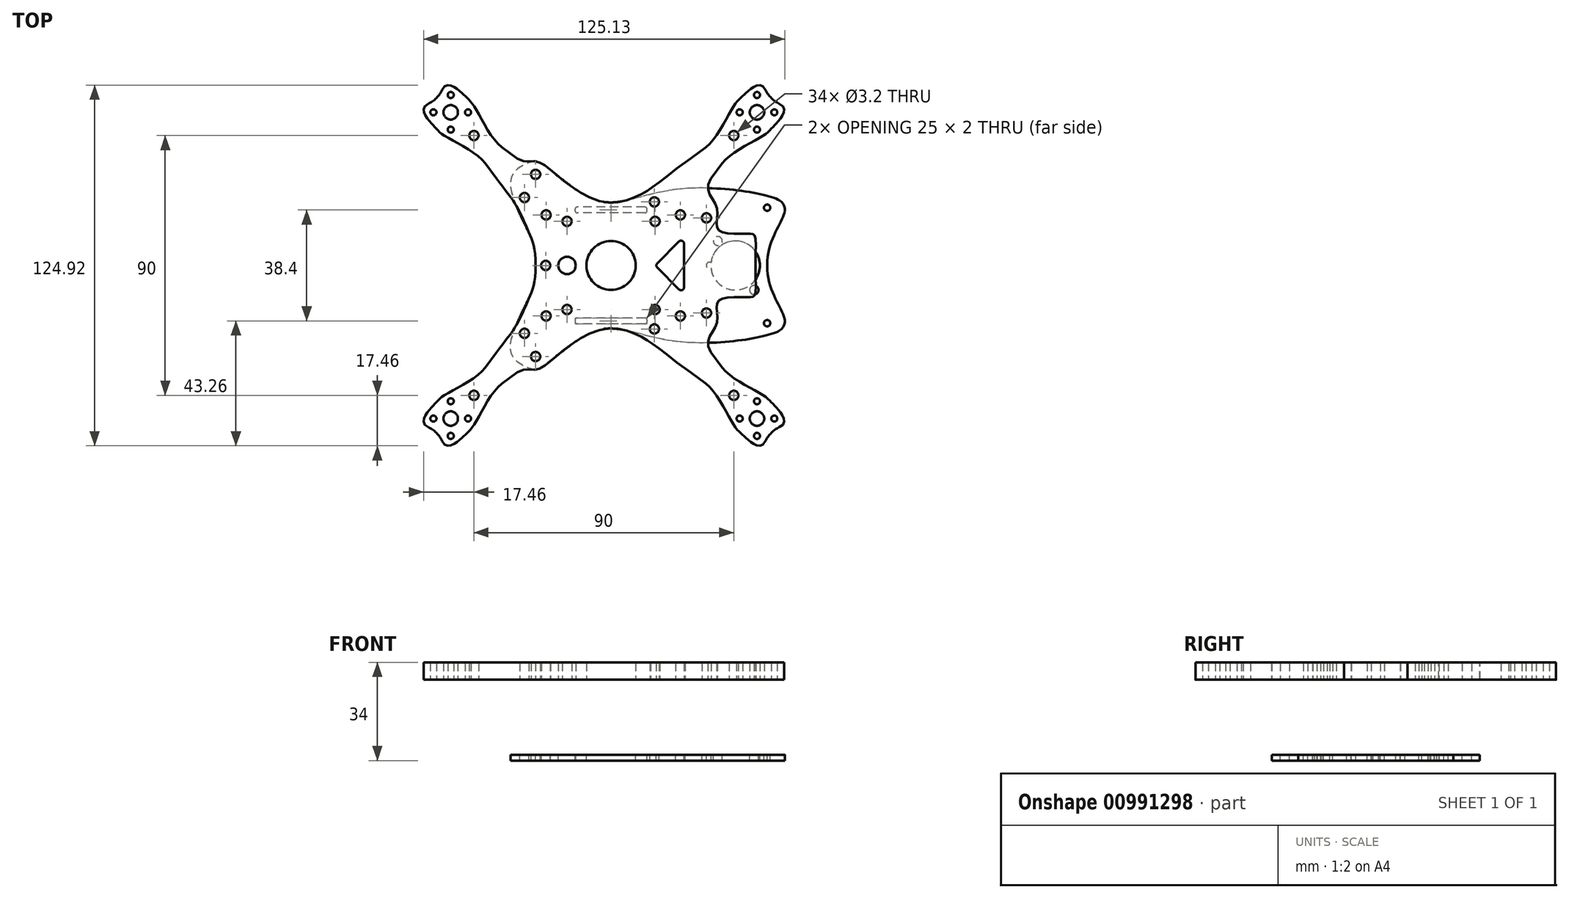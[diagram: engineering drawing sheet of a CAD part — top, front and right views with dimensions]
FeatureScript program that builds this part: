
annotation { "Feature Type Name" : "Feature", "Feature Type Description" : "" }
export const myFeature = defineFeature(function(context is Context, id is Id, definition is map)
    precondition{}
    {
        {
            var Q0;
            Q0=qCreatedBy(makeId("Top.planeOp"),FACE);
            var sketch = newSketch(context, id + "F0", { "sketchPlane" : qUnion([Q0])});
            skCircle(sketch, "E0", {"center": v(-47.03, 53.03) * mm, "radius": 1.05 * mm});
            skCircle(sketch, "E1", {"center": v(-53.03, 59.03) * mm, "radius": 1.05 * mm});
            skCircle(sketch, "E2", {"center": v(-59.03, 53.03) * mm, "radius": 1.05 * mm});
            skCircle(sketch, "E3", {"center": v(-53.03, 53.03) * mm, "radius": 2.5 * mm});
            skCircle(sketch, "E4", {"center": v(-53.03, 47.03) * mm, "radius": 1.05 * mm});
            skCircle(sketch, "E5", {"center": v(-45, 45) * mm, "radius": 1.6 * mm});
            skCircle(sketch, "E6", {"center": v(59.03, 53.03) * mm, "radius": 1.05 * mm});
            skCircle(sketch, "E7", {"center": v(53.03, 59.03) * mm, "radius": 1.05 * mm});
            skCircle(sketch, "E8", {"center": v(47.03, 53.03) * mm, "radius": 1.05 * mm});
            skCircle(sketch, "E9", {"center": v(53.03, 53.03) * mm, "radius": 2.5 * mm});
            skCircle(sketch, "E10", {"center": v(45, 45) * mm, "radius": 1.6 * mm});
            skCircle(sketch, "E11", {"center": v(53.03, 47.03) * mm, "radius": 1.05 * mm});
            skCircle(sketch, "E12", {"center": v(47.03, -53.03) * mm, "radius": 1.05 * mm});
            skCircle(sketch, "E13", {"center": v(45, -45) * mm, "radius": 1.6 * mm});
            skCircle(sketch, "E14", {"center": v(53.03, -47.03) * mm, "radius": 1.05 * mm});
            skCircle(sketch, "E15", {"center": v(53.03, -53.03) * mm, "radius": 2.5 * mm});
            skCircle(sketch, "E16", {"center": v(59.03, -53.03) * mm, "radius": 1.05 * mm});
            skCircle(sketch, "E17", {"center": v(53.03, -59.03) * mm, "radius": 1.05 * mm});
            skCircle(sketch, "E18", {"center": v(-27.5, 23.5) * mm, "radius": 1.6 * mm});
            skCircle(sketch, "E19", {"center": v(-27.5, -23.5) * mm, "radius": 1.6 * mm});
            skCircle(sketch, "E20", {"center": v(-23.64, -31.55) * mm, "radius": 1.6 * mm});
            skCircle(sketch, "E21", {"center": v(35.56, -16.47) * mm, "radius": 1.6 * mm});
            skCircle(sketch, "E22", {"center": v(35.56, 16.47) * mm, "radius": 1.6 * mm});
            skCircle(sketch, "E23", {"center": v(-23.64, 31.55) * mm, "radius": 1.6 * mm});
            skCircle(sketch, "E24", {"center": v(-20, 17.5) * mm, "radius": 1.6 * mm});
            skCircle(sketch, "E25", {"center": v(26.5, 17.5) * mm, "radius": 1.6 * mm});
            skCircle(sketch, "E26", {"center": v(26.5, -17.5) * mm, "radius": 1.6 * mm});
            skCircle(sketch, "E27", {"center": v(-20, -17.5) * mm, "radius": 1.6 * mm});
            skCircle(sketch, "E28", {"center": v(-45, -45) * mm, "radius": 1.6 * mm});
            skCircle(sketch, "E29", {"center": v(-53.03, -59.03) * mm, "radius": 1.05 * mm});
            skCircle(sketch, "E30", {"center": v(-59.03, -53.03) * mm, "radius": 1.05 * mm});
            skCircle(sketch, "E31", {"center": v(-53.03, -47.03) * mm, "radius": 1.05 * mm});
            skCircle(sketch, "E32", {"center": v(-53.03, -53.03) * mm, "radius": 2.5 * mm});
            skCircle(sketch, "E33", {"center": v(-47.03, -53.03) * mm, "radius": 1.05 * mm});
            skLineSegment(sketch, "E34", {"start": v(-37.07, 30) * mm, "end": v(-41.01, 35.36) * mm});
            skLineSegment(sketch, "E35", {"start": v(-35.36, 41.01) * mm, "end": v(-30, 37.07) * mm});
            skLineSegment(sketch, "E36", {"start": v(30, 37.07) * mm, "end": v(35.36, 41.01) * mm});
            skLineSegment(sketch, "E37", {"start": v(41.01, 35.36) * mm, "end": v(37.07, 30) * mm});
            skLineSegment(sketch, "E38", {"start": v(37.07, -30) * mm, "end": v(41.01, -35.36) * mm});
            skLineSegment(sketch, "E39", {"start": v(35.36, -41.01) * mm, "end": v(30, -37.07) * mm});
            skLineSegment(sketch, "E40", {"start": v(-30, -37.07) * mm, "end": v(-35.36, -41.01) * mm});
            skLineSegment(sketch, "E41", {"start": v(-41.01, -35.36) * mm, "end": v(-37.07, -30) * mm});
            skArc(sketch, "E42", {"start": v(-60.83, 56) * mm, "mid": v(-57.98, 57.98) * mm, "end": v(-56, 60.83) * mm});
            skPoint(sketch, "E43", {"position": v(2.5, 0) * mm});
            skLineSegment(sketch, "E44", {"start": v(0, 0) * mm, "end": v(-108.2, 108.2) * mm, "construction": true});
            skCircle(sketch, "E45", {"center": v(2.5, 0) * mm, "radius": 8.5 * mm});
            skLineSegment(sketch, "E46", {"start": v(-30, 37.07) * mm, "end": v(30, 37.07) * mm, "construction": true});
            skLineSegment(sketch, "E47", {"start": v(-37.07, 30) * mm, "end": v(-37.07, -30) * mm, "construction": true});
            skLineSegment(sketch, "E48", {"start": v(-30, -37.07) * mm, "end": v(30, -37.07) * mm, "construction": true});
            skLineSegment(sketch, "E49", {"start": v(37.07, -30) * mm, "end": v(37.07, 30) * mm, "construction": true});
            skLineSegment(sketch, "E50", {"start": v(-59.03, 53.03) * mm, "end": v(-47.03, 53.03) * mm, "construction": true});
            skLineSegment(sketch, "E51", {"start": v(-53.03, 47.03) * mm, "end": v(-53.03, 59.03) * mm, "construction": true});
            skCircle(sketch, "E52", {"center": v(-53.03, 53.03) * mm, "radius": 51.5 * mm, "construction": true});
            skLineSegment(sketch, "E53", {"start": v(-53.03, 53.03) * mm, "end": v(53.03, 53.03) * mm, "construction": true});
            skLineSegment(sketch, "E54", {"start": v(53.03, 53.03) * mm, "end": v(53.03, -53.03) * mm, "construction": true});
            skLineSegment(sketch, "E55", {"start": v(-53.03, -53.03) * mm, "end": v(53.03, -53.03) * mm, "construction": true});
            skLineSegment(sketch, "E56", {"start": v(-53.03, -53.03) * mm, "end": v(-53.03, 53.03) * mm, "construction": true});
            skLineSegment(sketch, "E57", {"start": v(0, 0) * mm, "end": v(53.03, 53.03) * mm, "construction": true});
            skLineSegment(sketch, "E58", {"start": v(-53.03, -53.03) * mm, "end": v(0, 0) * mm, "construction": true});
            skLineSegment(sketch, "E59", {"start": v(-41.01, 35.36) * mm, "end": v(-35.36, 41.01) * mm, "construction": true});
            skLineSegment(sketch, "E60", {"start": v(-37.07, 30) * mm, "end": v(-30, 37.07) * mm, "construction": true});
            skCircle(sketch, "E61", {"center": v(53.03, 53.03) * mm, "radius": 51.5 * mm, "construction": true});
            skCircle(sketch, "E62", {"center": v(53.03, -53.03) * mm, "radius": 51.5 * mm, "construction": true});
            skCircle(sketch, "E63", {"center": v(-53.03, -53.03) * mm, "radius": 51.5 * mm, "construction": true});
            skLineSegment(sketch, "E64", {"start": v(47.03, 53.03) * mm, "end": v(59.03, 53.03) * mm, "construction": true});
            skLineSegment(sketch, "E65", {"start": v(53.03, 47.03) * mm, "end": v(53.03, 59.03) * mm, "construction": true});
            skLineSegment(sketch, "E66", {"start": v(47.03, -53.03) * mm, "end": v(59.03, -53.03) * mm, "construction": true});
            skLineSegment(sketch, "E67", {"start": v(53.03, -47.03) * mm, "end": v(53.03, -59.03) * mm, "construction": true});
            skLineSegment(sketch, "E68", {"start": v(-59.03, -53.03) * mm, "end": v(-47.03, -53.03) * mm, "construction": true});
            skLineSegment(sketch, "E69", {"start": v(-53.03, -47.03) * mm, "end": v(-53.03, -59.03) * mm, "construction": true});
            skLineSegment(sketch, "E70", {"start": v(30, 37.07) * mm, "end": v(37.07, 30) * mm, "construction": true});
            skLineSegment(sketch, "E71", {"start": v(37.07, -30) * mm, "end": v(30, -37.07) * mm, "construction": true});
            skLineSegment(sketch, "E72", {"start": v(0, 0) * mm, "end": v(53.03, -53.03) * mm, "construction": true});
            skLineSegment(sketch, "E73", {"start": v(35.36, -41.01) * mm, "end": v(41.01, -35.36) * mm, "construction": true});
            skLineSegment(sketch, "E74", {"start": v(-35.36, -41.01) * mm, "end": v(-41.01, -35.36) * mm, "construction": true});
            skLineSegment(sketch, "E75", {"start": v(41.01, 35.36) * mm, "end": v(35.36, 41.01) * mm, "construction": true});
            skLineSegment(sketch, "E76", {"start": v(-56, 60.83) * mm, "end": v(-65.05, 65.05) * mm, "construction": true});
            skLineSegment(sketch, "E77", {"start": v(-60.83, 56) * mm, "end": v(-65.05, 65.05) * mm, "construction": true});
            skFitSpline(sketch, "E78", {"points": [v(-56, 60.83) * mm, v(-50.91, 61.15) * mm, v(-47.73, 58.34) * mm, v(-44.91, 55.15) * mm, v(-35.36, 41.01) * mm], "startDerivative": vector(17.72, 38) * mm, "endDerivative": vector(30.74, -22.62) * mm});
            skLineSegment(sketch, "E79", {"start": v(-56, 60.83) * mm, "end": v(-54.72, 63.55) * mm, "construction": true});
            skLineSegment(sketch, "E80", {"start": v(-39.38, 43.98) * mm, "end": v(-35.36, 41.01) * mm, "construction": true});
            skLineSegment(sketch, "E81", {"start": v(-53.03, 59.03) * mm, "end": v(-50.91, 61.15) * mm, "construction": true});
            skLineSegment(sketch, "E82", {"start": v(-47.03, 53.03) * mm, "end": v(-44.91, 55.15) * mm, "construction": true});
            skLineSegment(sketch, "E83", {"start": v(-53.03, 53.03) * mm, "end": v(-47.73, 58.34) * mm, "construction": true});
            skFitSpline(sketch, "E84.MirrorCS", {"points": [v(-60.83, 56) * mm, v(-61.15, 50.91) * mm, v(-58.34, 47.73) * mm, v(-55.15, 44.91) * mm, v(-41.01, 35.36) * mm], "startDerivative": vector(-38, -17.72) * mm, "endDerivative": vector(22.62, -30.74) * mm});
            skFitSpline(sketch, "E85.MirrorCS", {"points": [v(56, 60.83) * mm, v(50.91, 61.15) * mm, v(47.73, 58.34) * mm, v(44.91, 55.15) * mm, v(35.36, 41.01) * mm], "startDerivative": vector(-17.72, 38) * mm, "endDerivative": vector(-30.74, -22.62) * mm});
            skArc(sketch, "E86.MirrorCS", {"start": v(60.83, 56) * mm, "mid": v(57.98, 57.98) * mm, "end": v(56, 60.83) * mm});
            skFitSpline(sketch, "E87.MirrorCS", {"points": [v(60.83, 56) * mm, v(61.15, 50.91) * mm, v(58.34, 47.73) * mm, v(55.15, 44.91) * mm, v(41.01, 35.36) * mm], "startDerivative": vector(38, -17.72) * mm, "endDerivative": vector(-22.62, -30.74) * mm});
            skArc(sketch, "E88.MirrorCS", {"start": v(60.83, -56) * mm, "mid": v(57.98, -57.98) * mm, "end": v(56, -60.83) * mm});
            skFitSpline(sketch, "E89.MirrorCS", {"points": [v(60.83, -56) * mm, v(61.15, -50.91) * mm, v(58.34, -47.73) * mm, v(55.15, -44.91) * mm, v(41.01, -35.36) * mm], "startDerivative": vector(38, 17.72) * mm, "endDerivative": vector(-22.62, 30.74) * mm});
            skFitSpline(sketch, "E90.MirrorCS", {"points": [v(56, -60.83) * mm, v(50.91, -61.15) * mm, v(47.73, -58.34) * mm, v(44.91, -55.15) * mm, v(35.36, -41.01) * mm], "startDerivative": vector(-17.72, -38) * mm, "endDerivative": vector(-30.74, 22.62) * mm});
            skFitSpline(sketch, "E91.MirrorCS", {"points": [v(-56, -60.83) * mm, v(-50.91, -61.15) * mm, v(-47.73, -58.34) * mm, v(-44.91, -55.15) * mm, v(-35.36, -41.01) * mm], "startDerivative": vector(17.72, -38) * mm, "endDerivative": vector(30.74, 22.62) * mm});
            skArc(sketch, "E92.MirrorCS", {"start": v(-60.83, -56) * mm, "mid": v(-57.98, -57.98) * mm, "end": v(-56, -60.83) * mm});
            skFitSpline(sketch, "E93.MirrorCS", {"points": [v(-60.83, -56) * mm, v(-61.15, -50.91) * mm, v(-58.34, -47.73) * mm, v(-55.15, -44.91) * mm, v(-41.01, -35.36) * mm], "startDerivative": vector(-38, 17.72) * mm, "endDerivative": vector(22.62, 30.74) * mm});
            skLineSegment(sketch, "E94", {"start": v(19.53, 29.37) * mm, "end": v(30, 37.07) * mm, "construction": true});
            skLineSegment(sketch, "E95", {"start": v(-27.58, 35.3) * mm, "end": v(-30, 37.07) * mm, "construction": true});
            skLineSegment(sketch, "E96", {"start": v(-23.64, 31.55) * mm, "end": v(-23.64, 36.05) * mm, "construction": true});
            skLineSegment(sketch, "E97", {"start": v(-23.64, 31.55) * mm, "end": v(-16.64, 31.55) * mm, "construction": true});
            skLineSegment(sketch, "E98", {"start": v(-30, -37.07) * mm, "end": v(-37.07, -30) * mm, "construction": true});
            skLineSegment(sketch, "E99", {"start": v(-37.07, -30) * mm, "end": v(-34.1, -25.97) * mm, "construction": true});
            skLineSegment(sketch, "E100", {"start": v(-34.1, 25.97) * mm, "end": v(-37.07, 30) * mm, "construction": true});
            skLineSegment(sketch, "E101", {"start": v(-31.04, -19.96) * mm, "end": v(-27.5, -23.5) * mm, "construction": true});
            skLineSegment(sketch, "E102", {"start": v(-30.33, 20.67) * mm, "end": v(-27.5, 23.5) * mm, "construction": true});
            skLineSegment(sketch, "E103", {"start": v(34.1, 25.97) * mm, "end": v(37.07, 30) * mm, "construction": true});
            skLineSegment(sketch, "E104", {"start": v(35.56, 16.47) * mm, "end": v(39.1, 20) * mm, "construction": true});
            skLineSegment(sketch, "E105", {"start": v(52.5, 0) * mm, "end": v(52.5, 10) * mm, "construction": true});
            skFitSpline(sketch, "E106", {"points": [v(37.07, 30) * mm, v(39.1, 20) * mm, v(39.8, 12.23) * mm, v(50.5, 11) * mm, v(52.5, 0) * mm], "startDerivative": vector(-35.12, -47.72) * mm, "endDerivative": vector(0, -113.17) * mm});
            skLineSegment(sketch, "E107", {"start": v(35.56, 16.47) * mm, "end": v(39.8, 12.23) * mm, "construction": true});
            skLineSegment(sketch, "E108.bottom", {"start": v(17.75, 15.25) * mm, "end": v(-12.75, 15.25) * mm, "construction": true});
            skLineSegment(sketch, "E108.top", {"start": v(17.75, -15.25) * mm, "end": v(-12.75, -15.25) * mm, "construction": true});
            skLineSegment(sketch, "E108.left", {"start": v(17.75, 15.25) * mm, "end": v(17.75, -15.25) * mm, "construction": true});
            skLineSegment(sketch, "E108.right", {"start": v(-12.75, 15.25) * mm, "end": v(-12.75, -15.25) * mm, "construction": true});
            skCircle(sketch, "E109", {"center": v(-12.75, 15.25) * mm, "radius": 1.6 * mm});
            skCircle(sketch, "E110", {"center": v(17.75, 15.25) * mm, "radius": 1.6 * mm});
            skCircle(sketch, "E111", {"center": v(-12.75, -15.25) * mm, "radius": 1.6 * mm});
            skCircle(sketch, "E112", {"center": v(17.75, -15.25) * mm, "radius": 1.6 * mm});
            skFitSpline(sketch, "E113", {"points": [v(-30, 37.07) * mm, v(-23.64, 36.05) * mm, v(-16.64, 31.55) * mm, v(0, 22) * mm, v(13.5, 25) * mm, v(30, 37.07) * mm], "startDerivative": vector(51.54, -37.93) * mm, "endDerivative": vector(125.34, 92.24) * mm});
            skFitSpline(sketch, "E114.MirrorCS", {"points": [v(-30, -37.07) * mm, v(-23.64, -36.05) * mm, v(-16.64, -31.55) * mm, v(0, -22) * mm, v(13.5, -25) * mm, v(30, -37.07) * mm], "startDerivative": vector(51.54, 37.93) * mm, "endDerivative": vector(125.34, -92.24) * mm});
            skLineSegment(sketch, "E115", {"start": v(27.75, 0) * mm, "end": v(27.75, 7.59) * mm});
            skLineSegment(sketch, "E116", {"start": v(26.04, 8.3) * mm, "end": v(18.46, 0.7) * mm});
            skLineSegment(sketch, "E117", {"start": v(18.46, -0.7) * mm, "end": v(26.04, -8.3) * mm});
            skLineSegment(sketch, "E118", {"start": v(27.75, -7.59) * mm, "end": v(27.75, 0) * mm});
            skPoint(sketch, "E119.visualSharp", {"position": v(27.75, 10) * mm});
            skArc(sketch, "E119.filletArc", {"start": v(27.75, 7.59) * mm, "mid": v(27.13, 8.5) * mm, "end": v(26.04, 8.3) * mm});
            skPoint(sketch, "E120.visualSharp", {"position": v(27.75, -10) * mm});
            skArc(sketch, "E120.filletArc", {"start": v(26.04, -8.3) * mm, "mid": v(27.13, -8.5) * mm, "end": v(27.75, -7.59) * mm});
            skPoint(sketch, "E121.visualSharp", {"position": v(17.75, 0) * mm});
            skArc(sketch, "E121.filletArc", {"start": v(18.46, 0.7) * mm, "mid": v(18.16, 0) * mm, "end": v(18.46, -0.7) * mm});
            skCircle(sketch, "E122", {"center": v(-12.75, 0) * mm, "radius": 3 * mm});
            skFitSpline(sketch, "E123", {"points": [v(-37.07, 30) * mm, v(-30.33, 20.67) * mm, v(-26.01, 11.49) * mm, v(-23.64, 0) * mm], "startDerivative": vector(26.21, -35.62) * mm, "endDerivative": vector(0, -52.57) * mm});
            skLineSegment(sketch, "E124", {"start": v(-23.64, 0) * mm, "end": v(-23.64, 6) * mm, "construction": true});
            skLineSegment(sketch, "E125", {"start": v(-26.01, 11.49) * mm, "end": v(-20, 17.5) * mm, "construction": true});
            skFitSpline(sketch, "E126.MirrorCS", {"points": [v(-37.07, -30) * mm, v(-30.33, -20.67) * mm, v(-26.01, -11.49) * mm, v(-23.64, 0) * mm], "startDerivative": vector(26.21, 35.62) * mm, "endDerivative": vector(0, 52.57) * mm});
            skCircle(sketch, "E127", {"center": v(17.5, -22) * mm, "radius": 1.6 * mm});
            skCircle(sketch, "E128", {"center": v(-20.14, 0) * mm, "radius": 1.6 * mm});
            skCircle(sketch, "E129.MirrorC", {"center": v(17.5, 22) * mm, "radius": 1.6 * mm});
            skLineSegment(sketch, "E130", {"start": v(-45, -45) * mm, "end": v(45, -45) * mm, "construction": true});
            skLineSegment(sketch, "E131", {"start": v(45, 45) * mm, "end": v(45, -45) * mm, "construction": true});
            skLineSegment(sketch, "E132", {"start": v(-45, -45) * mm, "end": v(-45, 45) * mm, "construction": true});
            skLineSegment(sketch, "E133", {"start": v(-45, 45) * mm, "end": v(45, 45) * mm, "construction": true});
            skFitSpline(sketch, "E134.MirrorCS", {"points": [v(37.07, -30) * mm, v(39.1, -20) * mm, v(39.8, -12.23) * mm, v(50.5, -11) * mm, v(52.5, 0) * mm], "startDerivative": vector(-35.12, 47.72) * mm, "endDerivative": vector(0, 113.17) * mm});
            skSolve(sketch);
        }
        {
            var Q0;
            Q0 = qSketchRegion(id + "F0", true);
            extrude(context, id + "F1", {"entities" : qUnion([Q0]), "depth" : 6 * mm, "offsetDistance" : 25 * mm});
        }
        {
            var Q0;
            Q0=makeQuery(id+"F1.opExtrude","CAP_FACE",FACE,{"disambiguationData":[OSD([sQuery(id+"F0.wireOp",EDGE,"E0"),sQuery(id+"F0.wireOp",EDGE,"E1"),sQuery(id+"F0.wireOp",EDGE,"E2"),sQuery(id+"F0.wireOp",EDGE,"E3"),sQuery(id+"F0.wireOp",EDGE,"E4"),sQuery(id+"F0.wireOp",EDGE,"E5"),sQuery(id+"F0.wireOp",EDGE,"E6"),sQuery(id+"F0.wireOp",EDGE,"E7"),sQuery(id+"F0.wireOp",EDGE,"E8"),sQuery(id+"F0.wireOp",EDGE,"E9"),sQuery(id+"F0.wireOp",EDGE,"E10"),sQuery(id+"F0.wireOp",EDGE,"E11"),sQuery(id+"F0.wireOp",EDGE,"E12"),sQuery(id+"F0.wireOp",EDGE,"E13"),sQuery(id+"F0.wireOp",EDGE,"E14"),sQuery(id+"F0.wireOp",EDGE,"E15"),sQuery(id+"F0.wireOp",EDGE,"E16"),sQuery(id+"F0.wireOp",EDGE,"E17"),sQuery(id+"F0.wireOp",EDGE,"E18"),sQuery(id+"F0.wireOp",EDGE,"E19"),sQuery(id+"F0.wireOp",EDGE,"E20"),sQuery(id+"F0.wireOp",EDGE,"E21"),sQuery(id+"F0.wireOp",EDGE,"E22"),sQuery(id+"F0.wireOp",EDGE,"E23"),sQuery(id+"F0.wireOp",EDGE,"E24"),sQuery(id+"F0.wireOp",EDGE,"E25"),sQuery(id+"F0.wireOp",EDGE,"E26"),sQuery(id+"F0.wireOp",EDGE,"E27"),sQuery(id+"F0.wireOp",EDGE,"E28"),sQuery(id+"F0.wireOp",EDGE,"E29"),sQuery(id+"F0.wireOp",EDGE,"E30"),sQuery(id+"F0.wireOp",EDGE,"E31"),sQuery(id+"F0.wireOp",EDGE,"E32"),sQuery(id+"F0.wireOp",EDGE,"E33"),sQuery(id+"F0.wireOp",EDGE,"E34"),sQuery(id+"F0.wireOp",EDGE,"E35"),sQuery(id+"F0.wireOp",EDGE,"E36"),sQuery(id+"F0.wireOp",EDGE,"E37"),sQuery(id+"F0.wireOp",EDGE,"E38"),sQuery(id+"F0.wireOp",EDGE,"E39"),sQuery(id+"F0.wireOp",EDGE,"E40"),sQuery(id+"F0.wireOp",EDGE,"E41"),sQuery(id+"F0.wireOp",EDGE,"E42"),sQuery(id+"F0.wireOp",EDGE,"E45"),sQuery(id+"F0.wireOp",EDGE,"E78"),sQuery(id+"F0.wireOp",EDGE,"E84.MirrorCS"),sQuery(id+"F0.wireOp",EDGE,"E85.MirrorCS"),sQuery(id+"F0.wireOp",EDGE,"E86.MirrorCS"),sQuery(id+"F0.wireOp",EDGE,"E87.MirrorCS"),sQuery(id+"F0.wireOp",EDGE,"E88.MirrorCS"),sQuery(id+"F0.wireOp",EDGE,"E89.MirrorCS"),sQuery(id+"F0.wireOp",EDGE,"E90.MirrorCS"),sQuery(id+"F0.wireOp",EDGE,"E91.MirrorCS"),sQuery(id+"F0.wireOp",EDGE,"E92.MirrorCS"),sQuery(id+"F0.wireOp",EDGE,"E93.MirrorCS"),sQuery(id+"F0.wireOp",EDGE,"E106"),sQuery(id+"F0.wireOp",EDGE,"3d83afb9-14ca-451c-b238-5b0d7a678b5a0.MirrorCS"),sQuery(id+"F0.wireOp",EDGE,"E109"),sQuery(id+"F0.wireOp",EDGE,"E110"),sQuery(id+"F0.wireOp",EDGE,"E111"),sQuery(id+"F0.wireOp",EDGE,"E112"),sQuery(id+"F0.wireOp",EDGE,"E113"),sQuery(id+"F0.wireOp",EDGE,"E114.MirrorCS"),sQuery(id+"F0.wireOp",EDGE,"E115"),sQuery(id+"F0.wireOp",EDGE,"E116"),sQuery(id+"F0.wireOp",EDGE,"E117"),sQuery(id+"F0.wireOp",EDGE,"E118"),sQuery(id+"F0.wireOp",EDGE,"E119.filletArc"),sQuery(id+"F0.wireOp",EDGE,"E120.filletArc"),sQuery(id+"F0.wireOp",EDGE,"E121.filletArc"),sQuery(id+"F0.wireOp",EDGE,"E122"),sQuery(id+"F0.wireOp",EDGE,"E123"),sQuery(id+"F0.wireOp",EDGE,"E126.MirrorCS")])],"isStart":true});
            cPlane(context, id + "F2", {"entities" : qUnion([Q0]), "cplaneType" : CPlaneType.OFFSET, "offset" : 26 * mm, "width" : 150 * mm, "height" : 150 * mm});
        }
        {
            var Q0;
            Q0=qCreatedBy(id+"F2.planeOp",FACE);
            var sketch = newSketch(context, id + "F3", { "sketchPlane" : qUnion([Q0])});
            skCircle(sketch, "E135.0", {"center": v(35.56, 16.47) * mm, "radius": 1.6 * mm});
            skCircle(sketch, "E135.1", {"center": v(35.56, -16.47) * mm, "radius": 1.6 * mm});
            skCircle(sketch, "E135.2", {"center": v(-23.64, -31.55) * mm, "radius": 1.6 * mm});
            skCircle(sketch, "E135.3", {"center": v(-23.64, 31.55) * mm, "radius": 1.6 * mm});
            skFitSpline(sketch, "E136", {"points": [v(56.56, 0) * mm, v(61.56, -22) * mm], "startDerivative": vector(0, -36) * mm, "endDerivative": vector(-12.73, -12.73) * mm});
            skLineSegment(sketch, "E137", {"start": v(61.56, -22) * mm, "end": v(65.8, -17.76) * mm, "construction": true});
            skFitSpline(sketch, "E138", {"points": [v(61.56, -22) * mm, v(26.5, -26.5) * mm, v(0, -22) * mm, v(-16.64, -31.55) * mm, v(-23.64, -36.05) * mm], "startDerivative": vector(-26.25, -26.25) * mm, "endDerivative": vector(-19.13, 0) * mm});
            skLineSegment(sketch, "E139", {"start": v(58.73, -24.83) * mm, "end": v(61.56, -22) * mm, "construction": true});
            skLineSegment(sketch, "E140", {"start": v(-22.64, -36.05) * mm, "end": v(-23.64, -36.05) * mm, "construction": true});
            skFitSpline(sketch, "E141", {"points": [v(-23.64, -36.05) * mm, v(-31.55, -31.55) * mm, v(-30.33, -20.67) * mm, v(-26.01, -11.49) * mm, v(-23.64, 0) * mm], "startDerivative": vector(-25.73, 0) * mm, "endDerivative": vector(0, 67.98) * mm});
            skLineSegment(sketch, "E142", {"start": v(-25.64, -36.05) * mm, "end": v(-23.64, -36.05) * mm, "construction": true});
            skFitSpline(sketch, "E143.MirrorCS", {"points": [v(-23.64, 36.05) * mm, v(-31.55, 31.55) * mm, v(-30.33, 20.67) * mm, v(-26.01, 11.49) * mm, v(-23.64, 0) * mm], "startDerivative": vector(-25.73, 0) * mm, "endDerivative": vector(0, -67.98) * mm});
            skCircle(sketch, "E144.0", {"center": v(2.5, 0) * mm, "radius": 8.5 * mm});
            skCircle(sketch, "E145.1", {"center": v(-27.5, 23.5) * mm, "radius": 1.6 * mm});
            skCircle(sketch, "E145.2", {"center": v(-27.5, -23.5) * mm, "radius": 1.6 * mm});
            skCircle(sketch, "E146.1", {"center": v(17.5, 22) * mm, "radius": 1.6 * mm});
            skCircle(sketch, "E146.2", {"center": v(17.5, -22) * mm, "radius": 1.6 * mm});
            skLineSegment(sketch, "E147.bottom", {"start": v(48.5, 17.5) * mm, "end": v(-26.5, 17.5) * mm, "construction": true});
            skLineSegment(sketch, "E147.top", {"start": v(48.5, -17.5) * mm, "end": v(-26.5, -17.5) * mm, "construction": true});
            skLineSegment(sketch, "E147.left", {"start": v(48.5, 17.5) * mm, "end": v(48.5, -17.5) * mm, "construction": true});
            skLineSegment(sketch, "E147.right", {"start": v(-26.5, 17.5) * mm, "end": v(-26.5, -17.5) * mm, "construction": true});
            skPoint(sketch, "E147.middle", {"position": v(11, 0) * mm});
            skLineSegment(sketch, "E148.0", {"start": v(27.75, 0) * mm, "end": v(27.75, -7.59) * mm});
            skLineSegment(sketch, "E148.1", {"start": v(27.75, 7.59) * mm, "end": v(27.75, 0) * mm});
            skArc(sketch, "E148.2", {"start": v(26.04, 8.3) * mm, "mid": v(27.13, 8.5) * mm, "end": v(27.75, 7.59) * mm});
            skLineSegment(sketch, "E148.3", {"start": v(18.46, 0.7) * mm, "end": v(26.04, 8.3) * mm});
            skArc(sketch, "E148.4", {"start": v(18.46, -0.7) * mm, "mid": v(18.16, 0) * mm, "end": v(18.46, 0.7) * mm});
            skLineSegment(sketch, "E148.5", {"start": v(26.04, -8.3) * mm, "end": v(18.46, -0.7) * mm});
            skArc(sketch, "E148.6", {"start": v(27.75, -7.59) * mm, "mid": v(27.13, -8.5) * mm, "end": v(26.04, -8.3) * mm});
            skCircle(sketch, "E149.0", {"center": v(-20.14, 0) * mm, "radius": 1.6 * mm});
            skCircle(sketch, "E149.1", {"center": v(-12.75, 0) * mm, "radius": 3 * mm});
            skCircle(sketch, "E149.2", {"center": v(-20, 17.5) * mm, "radius": 1.6 * mm});
            skCircle(sketch, "E149.3", {"center": v(-20, -17.5) * mm, "radius": 1.6 * mm});
            skCircle(sketch, "E149.4", {"center": v(26.5, -17.5) * mm, "radius": 1.6 * mm});
            skCircle(sketch, "E149.5", {"center": v(26.5, 17.5) * mm, "radius": 1.6 * mm});
            skLineSegment(sketch, "E150.bottom", {"start": v(14.2, 18.2) * mm, "end": v(-9.2, 18.2) * mm});
            skLineSegment(sketch, "E150.top", {"start": v(14.2, 20.2) * mm, "end": v(-9.2, 20.2) * mm});
            skLineSegment(sketch, "E150.left", {"start": v(15, 19) * mm, "end": v(15, 19.4) * mm});
            skLineSegment(sketch, "E150.right", {"start": v(-10, 19) * mm, "end": v(-10, 19.4) * mm});
            skPoint(sketch, "E150.middle", {"position": v(2.5, 19.2) * mm});
            skPoint(sketch, "E151.visualSharp", {"position": v(-10, 20.2) * mm});
            skArc(sketch, "E151.filletArc", {"start": v(-9.2, 20.2) * mm, "mid": v(-9.77, 19.97) * mm, "end": v(-10, 19.4) * mm});
            skPoint(sketch, "E152.visualSharp", {"position": v(15, 20.2) * mm});
            skArc(sketch, "E152.filletArc", {"start": v(15, 19.4) * mm, "mid": v(14.77, 19.97) * mm, "end": v(14.2, 20.2) * mm});
            skPoint(sketch, "E153.visualSharp", {"position": v(-10, 18.2) * mm});
            skArc(sketch, "E153.filletArc", {"start": v(-10, 19) * mm, "mid": v(-9.77, 18.43) * mm, "end": v(-9.2, 18.2) * mm});
            skPoint(sketch, "E154.visualSharp", {"position": v(15, 18.2) * mm});
            skArc(sketch, "E154.filletArc", {"start": v(14.2, 18.2) * mm, "mid": v(14.77, 18.43) * mm, "end": v(15, 19) * mm});
            skLineSegment(sketch, "E155.MirrorCS", {"start": v(-10, -19) * mm, "end": v(-10, -19.4) * mm});
            skLineSegment(sketch, "E156.MirrorCS", {"start": v(15, -19) * mm, "end": v(15, -19.4) * mm});
            skArc(sketch, "E157.MirrorCS", {"start": v(15, -19.4) * mm, "mid": v(14.77, -19.97) * mm, "end": v(14.2, -20.2) * mm});
            skPoint(sketch, "E158.MirrorP", {"position": v(15, -20.2) * mm});
            skPoint(sketch, "E159.MirrorP", {"position": v(15, -18.2) * mm});
            skPoint(sketch, "E160.MirrorP", {"position": v(-10, -18.2) * mm});
            skPoint(sketch, "E161.MirrorP", {"position": v(-10, -20.2) * mm});
            skLineSegment(sketch, "E162.MirrorCS", {"start": v(14.2, -20.2) * mm, "end": v(-9.2, -20.2) * mm});
            skLineSegment(sketch, "E163.MirrorCS", {"start": v(14.2, -18.2) * mm, "end": v(-9.2, -18.2) * mm});
            skPoint(sketch, "E164.MirrorP", {"position": v(2.5, -19.2) * mm});
            skArc(sketch, "E165.MirrorCS", {"start": v(-9.2, -20.2) * mm, "mid": v(-9.77, -19.97) * mm, "end": v(-10, -19.4) * mm});
            skArc(sketch, "E166.MirrorCS", {"start": v(-10, -19) * mm, "mid": v(-9.77, -18.43) * mm, "end": v(-9.2, -18.2) * mm});
            skArc(sketch, "E167.MirrorCS", {"start": v(14.2, -18.2) * mm, "mid": v(14.77, -18.43) * mm, "end": v(15, -19) * mm});
            skCircle(sketch, "E168", {"center": v(45.56, 0) * mm, "radius": 8.5 * mm});
            skLineSegment(sketch, "E169", {"start": v(35.56, 16.47) * mm, "end": v(35.56, -16.47) * mm, "construction": true});
            skLineSegment(sketch, "E170", {"start": v(56.56, -12) * mm, "end": v(56.56, 0) * mm, "construction": true});
            skLineSegment(sketch, "E171.bottom", {"start": v(54.58, 11.05) * mm, "end": v(34.68, 11.05) * mm, "construction": true});
            skLineSegment(sketch, "E171.top", {"start": v(54.58, -11.05) * mm, "end": v(34.68, -11.05) * mm, "construction": true});
            skLineSegment(sketch, "E171.left", {"start": v(54.58, 11.05) * mm, "end": v(54.58, -11.05) * mm, "construction": true});
            skLineSegment(sketch, "E171.right", {"start": v(34.68, 11.05) * mm, "end": v(34.68, -11.05) * mm, "construction": true});
            skPoint(sketch, "E171.middle", {"position": v(44.63, 0) * mm});
            skCircle(sketch, "E172", {"center": v(52.04, 8.51) * mm, "radius": 1.55 * mm});
            skCircle(sketch, "E173", {"center": v(39.44, -8.49) * mm, "radius": 1.55 * mm});
            skCircle(sketch, "E174", {"center": v(56.56, 20) * mm, "radius": 1.1 * mm});
            skFitSpline(sketch, "E175.MirrorCS", {"points": [v(56.56, 0) * mm, v(61.56, 22) * mm], "startDerivative": vector(0, 36) * mm, "endDerivative": vector(-12.73, 12.73) * mm});
            skFitSpline(sketch, "E176.MirrorCS", {"points": [v(61.56, 22) * mm, v(26.5, 26.5) * mm, v(0, 22) * mm, v(-16.64, 31.55) * mm, v(-23.64, 36.05) * mm], "startDerivative": vector(-26.25, 26.25) * mm, "endDerivative": vector(-19.13, 0) * mm});
            skCircle(sketch, "E177.MirrorC", {"center": v(56.56, -20) * mm, "radius": 1.1 * mm});
            skCircle(sketch, "E178", {"center": v(36.56, 0) * mm, "radius": 1.1 * mm});
            skSolve(sketch);
        }
        {
            var Q0;
            Q0 = qSketchRegion(id + "F3", true);
            extrude(context, id + "F4", {"entities" : qUnion([Q0]), "depth" : 2 * mm, "offsetDistance" : 25 * mm});
        }
    });
